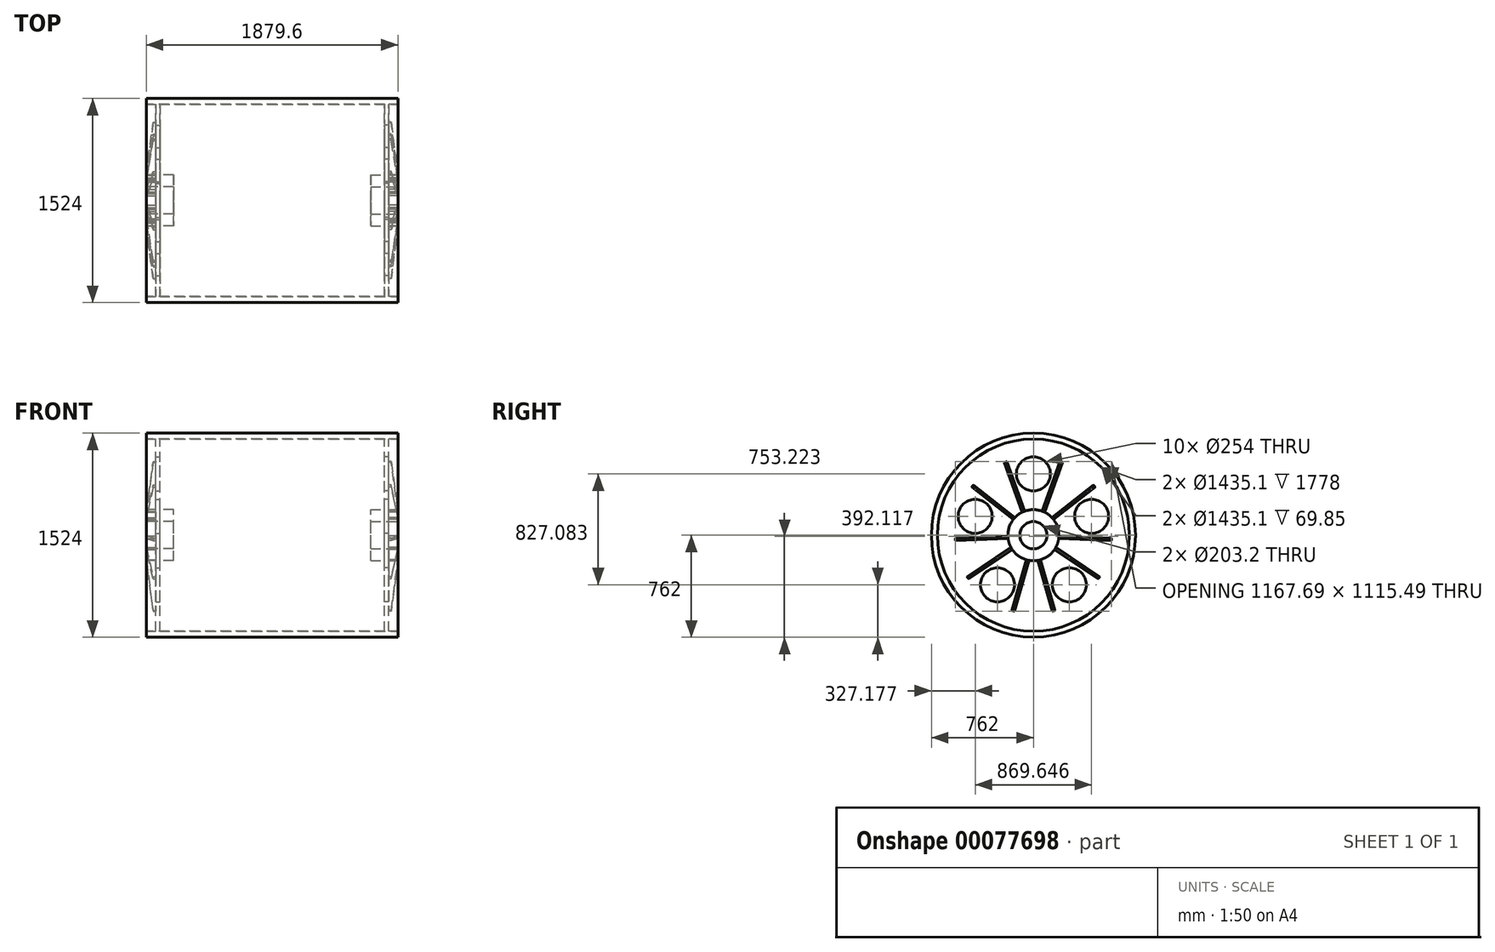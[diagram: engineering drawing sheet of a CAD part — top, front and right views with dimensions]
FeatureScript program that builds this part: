
annotation { "Feature Type Name" : "Feature", "Feature Type Description" : "" }
export const myFeature = defineFeature(function(context is Context, id is Id, definition is map)
    precondition{}
    {
        {
            var Q0;
            Q0=qCreatedBy(makeId("Right.planeOp"),FACE);
            var sketch = newSketch(context, id + "F0", { "sketchPlane" : qUnion([Q0])});
            skCircle(sketch, "E0", {"center": v(0, 0) * mm, "radius": 762 * mm});
            skCircle(sketch, "E1", {"center": v(0, 0) * mm, "radius": 717.55 * mm});
            skSolve(sketch);
        }
        {
            var Q0;
            Q0=qSketchRegion(id+"F0",true);
            extrude(context, id + "F1", {"entities" : qUnion([Q0]), "endBound" : BoundingType.SYMMETRIC, "depth" : 1879.6 * mm});
        }
        {
            var Q0;
            Q0=makeQuery(id+"F1.opExtrude","CAP_FACE",FACE,{"disambiguationData":[OSD([sQuery(id+"F0.wireOp",EDGE,"E0"),sQuery(id+"F0.wireOp",EDGE,"E1")])],"isStart":false});
            cPlane(context, id + "F2", {"entities" : qUnion([Q0]), "cplaneType" : CPlaneType.OFFSET, "offset" : 101.6 * mm, "oppositeDirection" : true, "width" : 152.4 * mm, "height" : 152.4 * mm});
        }
        {
            var Q0;
            Q0=qCreatedBy(id+"F2.planeOp",FACE);
            var sketch = newSketch(context, id + "F3", { "sketchPlane" : qUnion([Q0])});
            skCircle(sketch, "E2.0", {"center": v(0, 0) * mm, "radius": 717.55 * mm});
            skCircle(sketch, "E3", {"center": v(0, 0) * mm, "radius": 190.5 * mm});
            skCircle(sketch, "E4", {"center": v(0, 0) * mm, "radius": 457.2 * mm, "construction": true});
            skLineSegment(sketch, "E5", {"start": v(0, 0) * mm, "end": v(0, 568.44) * mm, "construction": true});
            skCircle(sketch, "E6", {"center": v(0, 457.2) * mm, "radius": 127 * mm});
            skCircle(sketch, "E7.1.0", {"center": v(-434.82, 141.28) * mm, "radius": 127 * mm});
            skCircle(sketch, "E7.2.0", {"center": v(-268.74, -369.88) * mm, "radius": 127 * mm});
            skCircle(sketch, "E8.1.3.0", {"center": v(268.74, -369.88) * mm, "radius": 127 * mm});
            skCircle(sketch, "E8.1.4.0", {"center": v(434.82, 141.28) * mm, "radius": 127 * mm});
            skSolve(sketch);
        }
        {
            var Q0;
            Q0=makeQuery(id+"F3.imprint","IMPRINT",FACE,{"disambiguationData":[TD([[makeQuery(id+"F3.imprint","IMPRINT",EDGE,{"derivedFrom":sQuery(id+"F3.wireOp",EDGE,"E2.0")}),1.0]])]});
            extrude(context, id + "F4", {"entities" : qUnion([Q0]), "operationType" : NewBodyOperationType.ADD, "depth" : 31.75 * mm});
        }
        {
            var Q0;
            Q0=makeQuery(id+"F4.opExtrude","CAP_FACE",FACE,{"disambiguationData":[OSD([sQuery(id+"F3.wireOp",EDGE,"E2.0"),sQuery(id+"F3.wireOp",EDGE,"E3"),sQuery(id+"F3.wireOp",EDGE,"E6"),sQuery(id+"F3.wireOp",EDGE,"E7.1.0"),sQuery(id+"F3.wireOp",EDGE,"E7.2.0"),sQuery(id+"F3.wireOp",EDGE,"E8.1.3.0"),sQuery(id+"F3.wireOp",EDGE,"E8.1.4.0")])],"isStart":false});
            var sketch = newSketch(context, id + "F5", { "sketchPlane" : qUnion([Q0])});
            skLineSegment(sketch, "E9", {"start": v(-65.15, 179.01) * mm, "end": v(-199.8, 548.97) * mm});
            skLineSegment(sketch, "E10", {"start": v(0, 0) * mm, "end": v(0, 828.08) * mm, "construction": true});
            skLineSegment(sketch, "E11.0", {"start": v(-82.73, 171.6) * mm, "end": v(-217.6, 542.16) * mm});
            skCircle(sketch, "E12.0", {"center": v(0, 0) * mm, "radius": 190.5 * mm, "construction": true});
            skArc(sketch, "E13.0", {"start": v(-199.8, 548.97) * mm, "mid": v(-208.73, 545.64) * mm, "end": v(-217.6, 542.16) * mm});
            skLineSegment(sketch, "E14", {"start": v(-65.15, 179.01) * mm, "end": v(-82.73, 171.6) * mm});
            skSolve(sketch);
        }
        {
            var Q0;
            Q0=qSketchRegion(id+"F5",true);
            var Q1;
            Q1=makeQuery(id+"F1.opExtrude","CAP_FACE",FACE,{"disambiguationData":[OSD([sQuery(id+"F0.wireOp",EDGE,"E0"),sQuery(id+"F0.wireOp",EDGE,"E1")])],"isStart":false});
            extrude(context, id + "F6", {"entities" : qUnion([Q0]), "endBound" : BoundingType.UP_TO_SURFACE, "endBoundEntityFace" : qUnion([Q1]), "depth" : 25.4 * mm});
        }
        {
            var Q0;
            Q0=makeQuery(id+"F6.opExtrude","SWEPT_FACE",FACE,{"disambiguationData":[OSD([sQuery(id+"F5.wireOp",EDGE,"E9")])]});
            var sketch = newSketch(context, id + "F7", { "sketchPlane" : qUnion([Q0])});
            skLineSegment(sketch, "E15.0", {"start": v(-889, -717.55) * mm, "end": v(-889, 717.55) * mm, "construction": true});
            skLineSegment(sketch, "E16.0", {"start": v(-939.8, 584.2) * mm, "end": v(-869.95, 584.2) * mm, "construction": true});
            skLineSegment(sketch, "E17.0", {"start": v(-939.8, 190.5) * mm, "end": v(-869.95, 190.5) * mm, "construction": true});
            skLineSegment(sketch, "E18", {"start": v(-889, 584.2) * mm, "end": v(-939.8, 190.5) * mm});
            skLineSegment(sketch, "E19", {"start": v(-889, 584.2) * mm, "end": v(-939.8, 584.2) * mm});
            skLineSegment(sketch, "E20", {"start": v(-939.8, 190.5) * mm, "end": v(-939.8, 584.2) * mm});
            skSolve(sketch);
        }
        {
            var Q0;
            Q0=qSketchRegion(id+"F7",true);
            extrude(context, id + "F8", {"entities" : qUnion([Q0]), "operationType" : NewBodyOperationType.REMOVE, "oppositeDirection" : true, "depth" : 50.8 * mm});
        }
        {
            var Q0;
            Q0=makeQuery(id+"F6.opExtrude","SWEPT_BODY",BODY,{"disambiguationData":[OSD([sQuery(id+"F5.wireOp",EDGE,"E9"),sQuery(id+"F5.wireOp",EDGE,"E11.0"),sQuery(id+"F5.wireOp",EDGE,"E13.0"),sQuery(id+"F5.wireOp",EDGE,"E14")])]});
            var Q1;
            Q1=qCreatedBy(makeId("Front.planeOp"),FACE);
            mirror(context, id + "F9", {"entities" : qUnion([Q0]), "mirrorPlane" : qUnion([Q1])});
        }
        {
            var Q0;
            Q0=makeQuery(id+"F6.opExtrude","SWEPT_BODY",BODY,{"disambiguationData":[OSD([sQuery(id+"F5.wireOp",EDGE,"E9"),sQuery(id+"F5.wireOp",EDGE,"E11.0"),sQuery(id+"F5.wireOp",EDGE,"E13.0"),sQuery(id+"F5.wireOp",EDGE,"E14")])]});
            var Q1;
            Q1=makeQuery(id+"F9.opPattern","COPY",BODY,{"derivedFrom":makeQuery(id+"F6.opExtrude","SWEPT_BODY",BODY,{"disambiguationData":[OSD([sQuery(id+"F5.wireOp",EDGE,"E9"),sQuery(id+"F5.wireOp",EDGE,"E11.0"),sQuery(id+"F5.wireOp",EDGE,"E13.0"),sQuery(id+"F5.wireOp",EDGE,"E14")])]}),"instanceName":"1"});
            var Q2;
            Q2=makeQuery(id+"F4.opExtrude","CAP_EDGE",EDGE,{"disambiguationData":[OSD([sQuery(id+"F3.wireOp",EDGE,"E3")])],"isStart":true});
            circularPattern(context, id + "F10", {"entities" : qUnion([Q0, Q1]), "axis" : qUnion([Q2]), "angle" : 72 * degree, "instanceCount" : 5});
        }
        {
            var Q0;
            Q0=makeQuery(id+"F1.opExtrude","CAP_FACE",FACE,{"disambiguationData":[OSD([sQuery(id+"F0.wireOp",EDGE,"E0"),sQuery(id+"F0.wireOp",EDGE,"E1")])],"isStart":false});
            var sketch = newSketch(context, id + "F11", { "sketchPlane" : qUnion([Q0])});
            skCircle(sketch, "E21", {"center": v(0, 0) * mm, "radius": 190.5 * mm});
            skCircle(sketch, "E22", {"center": v(0, 0) * mm, "radius": 101.6 * mm});
            skSolve(sketch);
        }
        {
            var Q0;
            Q0=qSketchRegion(id+"F11",true);
            extrude(context, id + "F12", {"entities" : qUnion([Q0]), "operationType" : NewBodyOperationType.ADD, "oppositeDirection" : true, "depth" : 203.2 * mm});
        }
        {
            var Q0;
            Q0=makeQuery(id+"F1.opExtrude","SWEPT_BODY",BODY,{"disambiguationData":[OSD([sQuery(id+"F0.wireOp",EDGE,"E0"),sQuery(id+"F0.wireOp",EDGE,"E1")])]});
            var Q1;
            Q1=makeQuery(id+"F4.opExtrude","SWEPT_FACE",FACE,{"disambiguationData":[OSD([sQuery(id+"F3.wireOp",EDGE,"E7.2.0")])]});
            var Q2;
            Q2=makeQuery(id+"F4.opExtrude","SWEPT_FACE",FACE,{"disambiguationData":[OSD([sQuery(id+"F3.wireOp",EDGE,"E6")])]});
            var Q3;
            Q3=makeQuery(id+"F4.opExtrude","SWEPT_FACE",FACE,{"disambiguationData":[OSD([sQuery(id+"F3.wireOp",EDGE,"E7.1.0")])]});
            var Q4;
            Q4=makeQuery(id+"F6.opExtrude","SWEPT_FACE",FACE,{"disambiguationData":[OSD([sQuery(id+"F5.wireOp",EDGE,"E11.0")])]});
            var Q5;
            {var subQ0=sQuery(id+"F11.wireOp",EDGE,"E21");var subQ5=makeQuery(id+"F8.boolean.opBoolean","COPY",FACE,{"derivedFrom":makeQuery(id+"F8.opExtrude","SWEPT_FACE",FACE,{"disambiguationData":[OSD([sQuery(id+"F7.wireOp",EDGE,"E18")])]})});Q5=makeQuery(id+"F12.boolean.opBoolean","SPLIT",FACE,{"disambiguationData":[TD([makeQuery(id+"F10.opPattern","COPY",FACE,{"derivedFrom":subQ5,"instanceName":"3"})])],"derivedFrom":makeQuery(id+"F12.opExtrude","SWEPT_FACE",FACE,{"disambiguationData":[OSD([subQ0])]})});}
            var Q6;
            Q6=makeQuery(id+"F4.opExtrude","CAP_FACE",FACE,{"disambiguationData":[OSD([sQuery(id+"F3.wireOp",EDGE,"E2.0"),sQuery(id+"F3.wireOp",EDGE,"E3"),sQuery(id+"F3.wireOp",EDGE,"E6"),sQuery(id+"F3.wireOp",EDGE,"E7.1.0"),sQuery(id+"F3.wireOp",EDGE,"E7.2.0"),sQuery(id+"F3.wireOp",EDGE,"E8.1.3.0"),sQuery(id+"F3.wireOp",EDGE,"E8.1.4.0")])],"isStart":true});
            var Q7;
            Q7=makeQuery(id+"F4.opExtrude","SWEPT_FACE",FACE,{"disambiguationData":[OSD([sQuery(id+"F3.wireOp",EDGE,"E8.1.3.0")])]});
            var Q8;
            Q8=makeQuery(id+"F4.opExtrude","SWEPT_FACE",FACE,{"disambiguationData":[OSD([sQuery(id+"F3.wireOp",EDGE,"E8.1.4.0")])]});
            var Q9;
            {var subQ3=makeQuery(id+"F6.opExtrude","SWEPT_FACE",FACE,{"disambiguationData":[OSD([sQuery(id+"F5.wireOp",EDGE,"E11.0")])]});var subQ4=sQuery(id+"F11.wireOp",EDGE,"E21");Q9=makeQuery(id+"F12.boolean.opBoolean","SPLIT",FACE,{"disambiguationData":[TD([makeQuery(id+"F10.opPattern","COPY",FACE,{"derivedFrom":subQ3,"instanceName":"2"})])],"derivedFrom":makeQuery(id+"F12.opExtrude","SWEPT_FACE",FACE,{"disambiguationData":[OSD([subQ4])]})});}
            var Q10;
            Q10=makeQuery(id+"F9.opPattern","COPY",FACE,{"derivedFrom":makeQuery(id+"F6.opExtrude","SWEPT_FACE",FACE,{"disambiguationData":[OSD([sQuery(id+"F5.wireOp",EDGE,"E13.0")])]}),"instanceName":"1"});
            var Q11;
            Q11=makeQuery(id+"F6.opExtrude","SWEPT_FACE",FACE,{"disambiguationData":[OSD([sQuery(id+"F5.wireOp",EDGE,"E13.0")])]});
            var Q12;
            Q12=makeQuery(id+"F8.boolean.opBoolean","COPY",FACE,{"derivedFrom":makeQuery(id+"F8.opExtrude","SWEPT_FACE",FACE,{"disambiguationData":[OSD([sQuery(id+"F7.wireOp",EDGE,"E18")])]})});
            var Q13;
            Q13=makeQuery(id+"F6.opExtrude","SWEPT_FACE",FACE,{"disambiguationData":[OSD([sQuery(id+"F5.wireOp",EDGE,"E9")])]});
            var Q14;
            {var subQ0=sQuery(id+"F0.wireOp",EDGE,"E1");Q14=makeQuery(id+"F4.boolean.opBoolean","SPLIT",FACE,{"disambiguationData":[TD([makeQuery(id+"F1.opExtrude","CAP_FACE",FACE,{"disambiguationData":[OSD([sQuery(id+"F0.wireOp",EDGE,"E0"),subQ0])],"isStart":false})])],"derivedFrom":makeQuery(id+"F1.opExtrude","SWEPT_FACE",FACE,{"disambiguationData":[OSD([subQ0])]})});}
            var Q15;
            Q15=makeQuery(id+"F1.opExtrude","CAP_FACE",FACE,{"disambiguationData":[OSD([sQuery(id+"F0.wireOp",EDGE,"E0"),sQuery(id+"F0.wireOp",EDGE,"E1")])],"isStart":false});
            var Q16;
            Q16=makeQuery(id+"F9.opPattern","COPY",FACE,{"derivedFrom":makeQuery(id+"F6.opExtrude","SWEPT_FACE",FACE,{"disambiguationData":[OSD([sQuery(id+"F5.wireOp",EDGE,"E9")])]}),"instanceName":"1"});
            var Q17;
            Q17=makeQuery(id+"F9.opPattern","COPY",FACE,{"derivedFrom":makeQuery(id+"F8.boolean.opBoolean","COPY",FACE,{"derivedFrom":makeQuery(id+"F8.opExtrude","SWEPT_FACE",FACE,{"disambiguationData":[OSD([sQuery(id+"F7.wireOp",EDGE,"E18")])]})}),"instanceName":"1"});
            var Q18;
            Q18=makeQuery(id+"F9.opPattern","COPY",FACE,{"derivedFrom":makeQuery(id+"F6.opExtrude","SWEPT_FACE",FACE,{"disambiguationData":[OSD([sQuery(id+"F5.wireOp",EDGE,"E11.0")])]}),"instanceName":"1"});
            var Q19;
            Q19=makeQuery(id+"F10.opPattern","COPY",FACE,{"derivedFrom":makeQuery(id+"F9.opPattern","COPY",FACE,{"derivedFrom":makeQuery(id+"F8.boolean.opBoolean","COPY",FACE,{"derivedFrom":makeQuery(id+"F8.opExtrude","SWEPT_FACE",FACE,{"disambiguationData":[OSD([sQuery(id+"F7.wireOp",EDGE,"E18")])]})}),"instanceName":"1"}),"instanceName":"4"});
            var Q20;
            Q20=makeQuery(id+"F10.opPattern","COPY",FACE,{"derivedFrom":makeQuery(id+"F9.opPattern","COPY",FACE,{"derivedFrom":makeQuery(id+"F6.opExtrude","SWEPT_FACE",FACE,{"disambiguationData":[OSD([sQuery(id+"F5.wireOp",EDGE,"E9")])]}),"instanceName":"1"}),"instanceName":"3"});
            var Q21;
            Q21=makeQuery(id+"F10.opPattern","COPY",FACE,{"derivedFrom":makeQuery(id+"F9.opPattern","COPY",FACE,{"derivedFrom":makeQuery(id+"F6.opExtrude","SWEPT_FACE",FACE,{"disambiguationData":[OSD([sQuery(id+"F5.wireOp",EDGE,"E11.0")])]}),"instanceName":"1"}),"instanceName":"4"});
            var Q22;
            Q22=makeQuery(id+"F10.opPattern","COPY",FACE,{"derivedFrom":makeQuery(id+"F6.opExtrude","SWEPT_FACE",FACE,{"disambiguationData":[OSD([sQuery(id+"F5.wireOp",EDGE,"E9")])]}),"instanceName":"4"});
            var Q23;
            Q23=makeQuery(id+"F10.opPattern","COPY",FACE,{"derivedFrom":makeQuery(id+"F8.boolean.opBoolean","COPY",FACE,{"derivedFrom":makeQuery(id+"F8.opExtrude","SWEPT_FACE",FACE,{"disambiguationData":[OSD([sQuery(id+"F7.wireOp",EDGE,"E18")])]})}),"instanceName":"1"});
            var Q24;
            {var subQ3=makeQuery(id+"F6.opExtrude","SWEPT_FACE",FACE,{"disambiguationData":[OSD([sQuery(id+"F5.wireOp",EDGE,"E11.0")])]});var subQ4=sQuery(id+"F11.wireOp",EDGE,"E21");Q24=makeQuery(id+"F12.boolean.opBoolean","SPLIT",FACE,{"disambiguationData":[TD([subQ3])],"derivedFrom":makeQuery(id+"F12.opExtrude","SWEPT_FACE",FACE,{"disambiguationData":[OSD([subQ4])]})});}
            var Q25;
            Q25=makeQuery(id+"F10.opPattern","COPY",FACE,{"derivedFrom":makeQuery(id+"F9.opPattern","COPY",FACE,{"derivedFrom":makeQuery(id+"F6.opExtrude","SWEPT_FACE",FACE,{"disambiguationData":[OSD([sQuery(id+"F5.wireOp",EDGE,"E13.0")])]}),"instanceName":"1"}),"instanceName":"1"});
            var Q26;
            Q26=makeQuery(id+"F12.opExtrude","CAP_FACE",FACE,{"disambiguationData":[OSD([sQuery(id+"F11.wireOp",EDGE,"E21"),sQuery(id+"F11.wireOp",EDGE,"E22")])],"isStart":false});
            var Q27;
            Q27=makeQuery(id+"F10.opPattern","COPY",FACE,{"derivedFrom":makeQuery(id+"F9.opPattern","COPY",FACE,{"derivedFrom":makeQuery(id+"F6.opExtrude","SWEPT_FACE",FACE,{"disambiguationData":[OSD([sQuery(id+"F5.wireOp",EDGE,"E9")])]}),"instanceName":"1"}),"instanceName":"4"});
            var Q28;
            Q28=makeQuery(id+"F10.opPattern","COPY",FACE,{"derivedFrom":makeQuery(id+"F6.opExtrude","SWEPT_FACE",FACE,{"disambiguationData":[OSD([sQuery(id+"F5.wireOp",EDGE,"E13.0")])]}),"instanceName":"3"});
            var Q29;
            Q29=makeQuery(id+"F4.opExtrude","CAP_FACE",FACE,{"disambiguationData":[OSD([sQuery(id+"F3.wireOp",EDGE,"E2.0"),sQuery(id+"F3.wireOp",EDGE,"E3"),sQuery(id+"F3.wireOp",EDGE,"E6"),sQuery(id+"F3.wireOp",EDGE,"E7.1.0"),sQuery(id+"F3.wireOp",EDGE,"E7.2.0"),sQuery(id+"F3.wireOp",EDGE,"E8.1.3.0"),sQuery(id+"F3.wireOp",EDGE,"E8.1.4.0")])],"isStart":false});
            var Q30;
            Q30=makeQuery(id+"F10.opPattern","COPY",FACE,{"derivedFrom":makeQuery(id+"F6.opExtrude","SWEPT_FACE",FACE,{"disambiguationData":[OSD([sQuery(id+"F5.wireOp",EDGE,"E11.0")])]}),"instanceName":"1"});
            var Q31;
            Q31=makeQuery(id+"F10.opPattern","COPY",FACE,{"derivedFrom":makeQuery(id+"F9.opPattern","COPY",FACE,{"derivedFrom":makeQuery(id+"F6.opExtrude","SWEPT_FACE",FACE,{"disambiguationData":[OSD([sQuery(id+"F5.wireOp",EDGE,"E11.0")])]}),"instanceName":"1"}),"instanceName":"2"});
            var Q32;
            Q32=makeQuery(id+"F10.opPattern","COPY",FACE,{"derivedFrom":makeQuery(id+"F6.opExtrude","SWEPT_FACE",FACE,{"disambiguationData":[OSD([sQuery(id+"F5.wireOp",EDGE,"E9")])]}),"instanceName":"1"});
            var Q33;
            {var subQ0=makeQuery(id+"F6.opExtrude","SWEPT_FACE",FACE,{"disambiguationData":[OSD([sQuery(id+"F5.wireOp",EDGE,"E9")])]});var subQ5=sQuery(id+"F11.wireOp",EDGE,"E21");Q33=makeQuery(id+"F12.boolean.opBoolean","SPLIT",FACE,{"disambiguationData":[TD([subQ0])],"derivedFrom":makeQuery(id+"F12.opExtrude","SWEPT_FACE",FACE,{"disambiguationData":[OSD([subQ5])]})});}
            var Q34;
            {var subQ0=sQuery(id+"F11.wireOp",EDGE,"E21");var subQ6=makeQuery(id+"F8.boolean.opBoolean","COPY",FACE,{"derivedFrom":makeQuery(id+"F8.opExtrude","SWEPT_FACE",FACE,{"disambiguationData":[OSD([sQuery(id+"F7.wireOp",EDGE,"E18")])]})});Q34=makeQuery(id+"F12.boolean.opBoolean","SPLIT",FACE,{"disambiguationData":[TD([makeQuery(id+"F10.opPattern","COPY",FACE,{"derivedFrom":subQ6,"instanceName":"2"})])],"derivedFrom":makeQuery(id+"F12.opExtrude","SWEPT_FACE",FACE,{"disambiguationData":[OSD([subQ0])]})});}
            var Q35;
            Q35=makeQuery(id+"F10.opPattern","COPY",FACE,{"derivedFrom":makeQuery(id+"F6.opExtrude","SWEPT_FACE",FACE,{"disambiguationData":[OSD([sQuery(id+"F5.wireOp",EDGE,"E11.0")])]}),"instanceName":"2"});
            var Q36;
            Q36=makeQuery(id+"F10.opPattern","COPY",FACE,{"derivedFrom":makeQuery(id+"F6.opExtrude","SWEPT_FACE",FACE,{"disambiguationData":[OSD([sQuery(id+"F5.wireOp",EDGE,"E11.0")])]}),"instanceName":"4"});
            var Q37;
            Q37=makeQuery(id+"F10.opPattern","COPY",FACE,{"derivedFrom":makeQuery(id+"F6.opExtrude","SWEPT_FACE",FACE,{"disambiguationData":[OSD([sQuery(id+"F5.wireOp",EDGE,"E9")])]}),"instanceName":"3"});
            var Q38;
            Q38=makeQuery(id+"F10.opPattern","COPY",FACE,{"derivedFrom":makeQuery(id+"F9.opPattern","COPY",FACE,{"derivedFrom":makeQuery(id+"F6.opExtrude","SWEPT_FACE",FACE,{"disambiguationData":[OSD([sQuery(id+"F5.wireOp",EDGE,"E11.0")])]}),"instanceName":"1"}),"instanceName":"1"});
            var Q39;
            Q39=makeQuery(id+"F10.opPattern","COPY",FACE,{"derivedFrom":makeQuery(id+"F9.opPattern","COPY",FACE,{"derivedFrom":makeQuery(id+"F8.boolean.opBoolean","COPY",FACE,{"derivedFrom":makeQuery(id+"F8.opExtrude","SWEPT_FACE",FACE,{"disambiguationData":[OSD([sQuery(id+"F7.wireOp",EDGE,"E18")])]})}),"instanceName":"1"}),"instanceName":"1"});
            var Q40;
            {var subQ0=makeQuery(id+"F6.opExtrude","CAP_FACE",FACE,{"disambiguationData":[OSD([sQuery(id+"F0.wireOp",EDGE,"E0"),sQuery(id+"F0.wireOp",EDGE,"E1")])],"isStart":false});var subQ1=makeQuery(id+"F9.opPattern","COPY",FACE,{"derivedFrom":subQ0,"instanceName":"1"});Q40=makeQuery(id+"F12.boolean.opBoolean","MERGE",FACE,{"derivedFrom":[subQ0,subQ1,makeQuery(id+"F10.opPattern","COPY",FACE,{"derivedFrom":subQ0,"instanceName":"1"}),makeQuery(id+"F10.opPattern","COPY",FACE,{"derivedFrom":subQ1,"instanceName":"1"}),makeQuery(id+"F10.opPattern","COPY",FACE,{"derivedFrom":subQ0,"instanceName":"2"}),makeQuery(id+"F10.opPattern","COPY",FACE,{"derivedFrom":subQ1,"instanceName":"2"}),makeQuery(id+"F10.opPattern","COPY",FACE,{"derivedFrom":subQ0,"instanceName":"3"}),makeQuery(id+"F10.opPattern","COPY",FACE,{"derivedFrom":subQ1,"instanceName":"3"}),makeQuery(id+"F10.opPattern","COPY",FACE,{"derivedFrom":subQ0,"instanceName":"4"}),makeQuery(id+"F10.opPattern","COPY",FACE,{"derivedFrom":subQ1,"instanceName":"4"}),makeQuery(id+"F12.opExtrude","CAP_FACE",FACE,{"disambiguationData":[OSD([sQuery(id+"F11.wireOp",EDGE,"E21"),sQuery(id+"F11.wireOp",EDGE,"E22")])],"isStart":true})]});}
            var Q41;
            Q41=makeQuery(id+"F10.opPattern","COPY",FACE,{"derivedFrom":makeQuery(id+"F9.opPattern","COPY",FACE,{"derivedFrom":makeQuery(id+"F6.opExtrude","SWEPT_FACE",FACE,{"disambiguationData":[OSD([sQuery(id+"F5.wireOp",EDGE,"E9")])]}),"instanceName":"1"}),"instanceName":"1"});
            var Q42;
            Q42=makeQuery(id+"F10.opPattern","COPY",FACE,{"derivedFrom":makeQuery(id+"F9.opPattern","COPY",FACE,{"derivedFrom":makeQuery(id+"F6.opExtrude","SWEPT_FACE",FACE,{"disambiguationData":[OSD([sQuery(id+"F5.wireOp",EDGE,"E9")])]}),"instanceName":"1"}),"instanceName":"2"});
            var Q43;
            {var subQ2=makeQuery(id+"F6.opExtrude","SWEPT_FACE",FACE,{"disambiguationData":[OSD([sQuery(id+"F5.wireOp",EDGE,"E11.0")])]});var subQ4=sQuery(id+"F11.wireOp",EDGE,"E21");Q43=makeQuery(id+"F12.boolean.opBoolean","SPLIT",FACE,{"disambiguationData":[TD([makeQuery(id+"F10.opPattern","COPY",FACE,{"derivedFrom":subQ2,"instanceName":"1"})])],"derivedFrom":makeQuery(id+"F12.opExtrude","SWEPT_FACE",FACE,{"disambiguationData":[OSD([subQ4])]})});}
            var Q44;
            {var subQ0=sQuery(id+"F11.wireOp",EDGE,"E21");var subQ6=makeQuery(id+"F8.boolean.opBoolean","COPY",FACE,{"derivedFrom":makeQuery(id+"F8.opExtrude","SWEPT_FACE",FACE,{"disambiguationData":[OSD([sQuery(id+"F7.wireOp",EDGE,"E18")])]})});Q44=makeQuery(id+"F12.boolean.opBoolean","SPLIT",FACE,{"disambiguationData":[TD([makeQuery(id+"F10.opPattern","COPY",FACE,{"derivedFrom":subQ6,"instanceName":"4"})])],"derivedFrom":makeQuery(id+"F12.opExtrude","SWEPT_FACE",FACE,{"disambiguationData":[OSD([subQ0])]})});}
            var Q45;
            Q45=makeQuery(id+"F10.opPattern","COPY",FACE,{"derivedFrom":makeQuery(id+"F9.opPattern","COPY",FACE,{"derivedFrom":makeQuery(id+"F6.opExtrude","SWEPT_FACE",FACE,{"disambiguationData":[OSD([sQuery(id+"F5.wireOp",EDGE,"E13.0")])]}),"instanceName":"1"}),"instanceName":"2"});
            var Q46;
            {var subQ0=makeQuery(id+"F6.opExtrude","SWEPT_FACE",FACE,{"disambiguationData":[OSD([sQuery(id+"F5.wireOp",EDGE,"E11.0")])]});var subQ4=sQuery(id+"F11.wireOp",EDGE,"E21");Q46=makeQuery(id+"F12.boolean.opBoolean","SPLIT",FACE,{"disambiguationData":[TD([makeQuery(id+"F10.opPattern","COPY",FACE,{"derivedFrom":subQ0,"instanceName":"3"})])],"derivedFrom":makeQuery(id+"F12.opExtrude","SWEPT_FACE",FACE,{"disambiguationData":[OSD([subQ4])]})});}
            var Q47;
            Q47=makeQuery(id+"F10.opPattern","COPY",FACE,{"derivedFrom":makeQuery(id+"F6.opExtrude","SWEPT_FACE",FACE,{"disambiguationData":[OSD([sQuery(id+"F5.wireOp",EDGE,"E9")])]}),"instanceName":"2"});
            var Q48;
            Q48=makeQuery(id+"F10.opPattern","COPY",FACE,{"derivedFrom":makeQuery(id+"F6.opExtrude","SWEPT_FACE",FACE,{"disambiguationData":[OSD([sQuery(id+"F5.wireOp",EDGE,"E11.0")])]}),"instanceName":"3"});
            var Q49;
            Q49=makeQuery(id+"F10.opPattern","COPY",FACE,{"derivedFrom":makeQuery(id+"F9.opPattern","COPY",FACE,{"derivedFrom":makeQuery(id+"F6.opExtrude","SWEPT_FACE",FACE,{"disambiguationData":[OSD([sQuery(id+"F5.wireOp",EDGE,"E13.0")])]}),"instanceName":"1"}),"instanceName":"4"});
            var Q50;
            Q50=makeQuery(id+"F10.opPattern","COPY",FACE,{"derivedFrom":makeQuery(id+"F9.opPattern","COPY",FACE,{"derivedFrom":makeQuery(id+"F8.boolean.opBoolean","COPY",FACE,{"derivedFrom":makeQuery(id+"F8.opExtrude","SWEPT_FACE",FACE,{"disambiguationData":[OSD([sQuery(id+"F7.wireOp",EDGE,"E18")])]})}),"instanceName":"1"}),"instanceName":"2"});
            var Q51;
            {var subQ3=sQuery(id+"F11.wireOp",EDGE,"E21");var subQ4=makeQuery(id+"F6.opExtrude","SWEPT_FACE",FACE,{"disambiguationData":[OSD([sQuery(id+"F5.wireOp",EDGE,"E11.0")])]});Q51=makeQuery(id+"F12.boolean.opBoolean","SPLIT",FACE,{"disambiguationData":[TD([makeQuery(id+"F9.opPattern","COPY",FACE,{"derivedFrom":subQ4,"instanceName":"1"})])],"derivedFrom":makeQuery(id+"F12.opExtrude","SWEPT_FACE",FACE,{"disambiguationData":[OSD([subQ3])]})});}
            var Q52;
            Q52=makeQuery(id+"F10.opPattern","COPY",FACE,{"derivedFrom":makeQuery(id+"F8.boolean.opBoolean","COPY",FACE,{"derivedFrom":makeQuery(id+"F8.opExtrude","SWEPT_FACE",FACE,{"disambiguationData":[OSD([sQuery(id+"F7.wireOp",EDGE,"E18")])]})}),"instanceName":"3"});
            var Q53;
            Q53=makeQuery(id+"F10.opPattern","COPY",FACE,{"derivedFrom":makeQuery(id+"F8.boolean.opBoolean","COPY",FACE,{"derivedFrom":makeQuery(id+"F8.opExtrude","SWEPT_FACE",FACE,{"disambiguationData":[OSD([sQuery(id+"F7.wireOp",EDGE,"E18")])]})}),"instanceName":"4"});
            var Q54;
            Q54=makeQuery(id+"F10.opPattern","COPY",FACE,{"derivedFrom":makeQuery(id+"F6.opExtrude","SWEPT_FACE",FACE,{"disambiguationData":[OSD([sQuery(id+"F5.wireOp",EDGE,"E13.0")])]}),"instanceName":"4"});
            var Q55;
            Q55=makeQuery(id+"F10.opPattern","COPY",FACE,{"derivedFrom":makeQuery(id+"F8.boolean.opBoolean","COPY",FACE,{"derivedFrom":makeQuery(id+"F8.opExtrude","SWEPT_FACE",FACE,{"disambiguationData":[OSD([sQuery(id+"F7.wireOp",EDGE,"E18")])]})}),"instanceName":"2"});
            var Q56;
            Q56=makeQuery(id+"F10.opPattern","COPY",FACE,{"derivedFrom":makeQuery(id+"F9.opPattern","COPY",FACE,{"derivedFrom":makeQuery(id+"F8.boolean.opBoolean","COPY",FACE,{"derivedFrom":makeQuery(id+"F8.opExtrude","SWEPT_FACE",FACE,{"disambiguationData":[OSD([sQuery(id+"F7.wireOp",EDGE,"E18")])]})}),"instanceName":"1"}),"instanceName":"3"});
            var Q57;
            Q57=makeQuery(id+"F12.opExtrude","SWEPT_FACE",FACE,{"disambiguationData":[OSD([sQuery(id+"F11.wireOp",EDGE,"E22")])]});
            var Q58;
            Q58=makeQuery(id+"F10.opPattern","COPY",FACE,{"derivedFrom":makeQuery(id+"F9.opPattern","COPY",FACE,{"derivedFrom":makeQuery(id+"F6.opExtrude","SWEPT_FACE",FACE,{"disambiguationData":[OSD([sQuery(id+"F5.wireOp",EDGE,"E13.0")])]}),"instanceName":"1"}),"instanceName":"3"});
            var Q59;
            Q59=makeQuery(id+"F10.opPattern","COPY",FACE,{"derivedFrom":makeQuery(id+"F6.opExtrude","SWEPT_FACE",FACE,{"disambiguationData":[OSD([sQuery(id+"F5.wireOp",EDGE,"E13.0")])]}),"instanceName":"2"});
            var Q60;
            {var subQ0=sQuery(id+"F11.wireOp",EDGE,"E21");var subQ6=makeQuery(id+"F8.boolean.opBoolean","COPY",FACE,{"derivedFrom":makeQuery(id+"F8.opExtrude","SWEPT_FACE",FACE,{"disambiguationData":[OSD([sQuery(id+"F7.wireOp",EDGE,"E18")])]})});Q60=makeQuery(id+"F12.boolean.opBoolean","SPLIT",FACE,{"disambiguationData":[TD([makeQuery(id+"F10.opPattern","COPY",FACE,{"derivedFrom":subQ6,"instanceName":"1"})])],"derivedFrom":makeQuery(id+"F12.opExtrude","SWEPT_FACE",FACE,{"disambiguationData":[OSD([subQ0])]})});}
            var Q61;
            Q61=makeQuery(id+"F10.opPattern","COPY",FACE,{"derivedFrom":makeQuery(id+"F6.opExtrude","SWEPT_FACE",FACE,{"disambiguationData":[OSD([sQuery(id+"F5.wireOp",EDGE,"E13.0")])]}),"instanceName":"1"});
            var Q62;
            {var subQ0=sQuery(id+"F11.wireOp",EDGE,"E21");Q62=makeQuery(id+"F12.boolean.opBoolean","SPLIT",FACE,{"disambiguationData":[TD([makeQuery(id+"F12.opExtrude","CAP_FACE",FACE,{"disambiguationData":[OSD([subQ0,sQuery(id+"F11.wireOp",EDGE,"E22")])],"isStart":false})])],"derivedFrom":makeQuery(id+"F12.opExtrude","SWEPT_FACE",FACE,{"disambiguationData":[OSD([subQ0])]})});}
            var Q63;
            Q63=makeQuery(id+"F10.opPattern","COPY",FACE,{"derivedFrom":makeQuery(id+"F9.opPattern","COPY",FACE,{"derivedFrom":makeQuery(id+"F6.opExtrude","SWEPT_FACE",FACE,{"disambiguationData":[OSD([sQuery(id+"F5.wireOp",EDGE,"E11.0")])]}),"instanceName":"1"}),"instanceName":"3"});
            var Q64;
            Q64=qCreatedBy(makeId("Right.planeOp"),FACE);
            mirror(context, id + "F13", {"entities" : qUnion([Q0]), "faces" : qUnion([Q1, Q2, Q3, Q4, Q5, Q6, Q7, Q8, Q9, Q10, Q11, Q12, Q13, Q14, Q15, Q16, Q17, Q18, Q19, Q20, Q21, Q22, Q23, Q24, Q25, Q26, Q27, Q28, Q29, Q30, Q31, Q32, Q33, Q34, Q35, Q36, Q37, Q38, Q39, Q40, Q41, Q42, Q43, Q44, Q45, Q46, Q47, Q48, Q49, Q50, Q51, Q52, Q53, Q54, Q55, Q56, Q57, Q58, Q59, Q60, Q61, Q62, Q63]), "mirrorPlane" : qUnion([Q64])});
        }
    });
